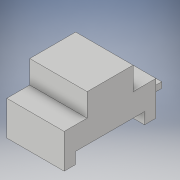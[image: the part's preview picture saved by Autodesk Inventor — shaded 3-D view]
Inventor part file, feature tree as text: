
AUTODESK INVENTOR PART (.ipt)
format: ipt  version: 2018 (Build 220112000, 112)  size: 125,952 bytes
history: native  units: in
note: dims shown in document units (in); Inventor stores cm internally (conversion verified against a paired STEP export)
features: extrude x4, sketch x4
ambient origin geometry x8: Origin, YZ Plane, XZ Plane, XY Plane, X Axis, Y Axis, Z Axis, Center Point
bodies: Solid1 (feature_tree)
feature tree (8):
  extrude  "Extrusion1"  Depth=4.0in
  extrude  "Extrusion2"  Depth=0.5in
  extrude  "Extrusion3"  Depth=0.5in TaperAngle=0.0deg
  extrude  "Extrusion4"  Depth=2.0in
  sketch  "Sketch1"  dims[d0=2.5in d1=4.0in]
  sketch  "Sketch2"  dims[d2=1.5in d3=0.0in d4=0.5in]
  sketch  "Sketch3"  dims[d5=3.0in d6=0.5in d7=0.0in]
  sketch  "Sketch4"  dims[d8=1.0in d9=2.0in d10=1.0in d11=0.0in d12=0.5in d13=0.75in d14=1.5in d15=0.25in d16=0.75in d17=0.0in]
